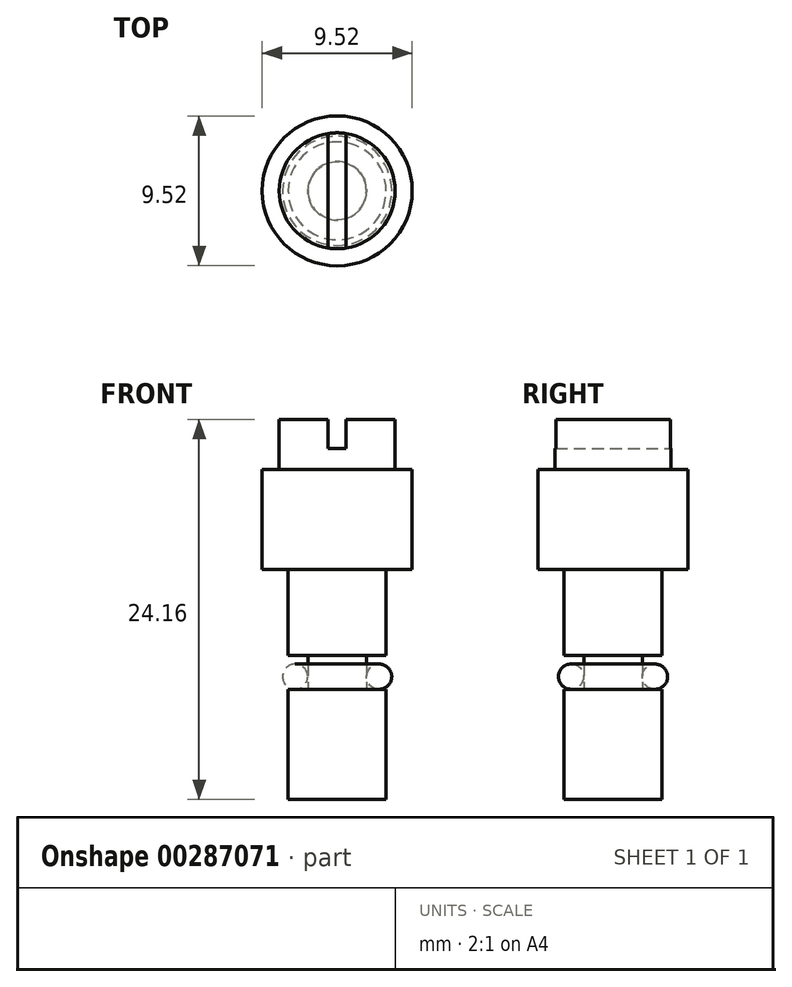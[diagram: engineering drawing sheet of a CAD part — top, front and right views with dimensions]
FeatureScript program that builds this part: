
annotation { "Feature Type Name" : "Feature", "Feature Type Description" : "" }
export const myFeature = defineFeature(function(context is Context, id is Id, definition is map)
    precondition{}
    {
        {
            var Q0;
            Q0=qCreatedBy(makeId("Front.planeOp"),FACE);
            var sketch = newSketch(context, id + "F0", { "sketchPlane" : qUnion([Q0])});
            skLineSegment(sketch, "E0", {"start": v(0, 0) * mm, "end": v(0, 26.45) * mm, "construction": true});
            skLineSegment(sketch, "E1", {"start": v(0, 0) * mm, "end": v(3.11, 0) * mm});
            skLineSegment(sketch, "E2", {"start": v(3.11, 0) * mm, "end": v(3.11, 7.01) * mm});
            skLineSegment(sketch, "E3", {"start": v(3.11, 7.01) * mm, "end": v(1.85, 7.01) * mm});
            skLineSegment(sketch, "E4", {"start": v(1.85, 7.01) * mm, "end": v(1.85, 9.17) * mm});
            skLineSegment(sketch, "E5", {"start": v(1.85, 9.17) * mm, "end": v(3.11, 9.17) * mm});
            skLineSegment(sketch, "E6", {"start": v(3.11, 9.17) * mm, "end": v(3.11, 14.63) * mm});
            skLineSegment(sketch, "E7", {"start": v(3.11, 14.63) * mm, "end": v(4.76, 14.63) * mm});
            skLineSegment(sketch, "E8", {"start": v(4.76, 14.63) * mm, "end": v(4.76, 20.98) * mm});
            skLineSegment(sketch, "E9", {"start": v(0, 24.16) * mm, "end": v(0, 0) * mm});
            skLineSegment(sketch, "E10", {"start": v(0, 24.16) * mm, "end": v(3.68, 24.16) * mm});
            skLineSegment(sketch, "E11", {"start": v(3.68, 24.16) * mm, "end": v(3.68, 20.98) * mm});
            skLineSegment(sketch, "E12", {"start": v(3.68, 20.98) * mm, "end": v(4.76, 20.98) * mm});
            skSolve(sketch);
        }
        {
            var Q0;
            Q0 = qSketchRegion(id + "F0", true);
            var Q1;
            Q1=sQuery(id+"F0.wireOp",EDGE,"E0");
            revolve(context, id + "F1", {"entities" : qUnion([Q0]), "axis" : qUnion([Q1]), "revolveType" : RevolveType.FULL});
        }
        {
            var Q0;
            Q0=makeQuery(id+"F1.opRevolve","SWEPT_FACE",FACE,{"disambiguationData":[OSD([sQuery(id+"F0.wireOp",EDGE,"E10")])]});
            var sketch = newSketch(context, id + "F2", { "sketchPlane" : qUnion([Q0])});
            skLineSegment(sketch, "E13.bottom", {"start": v(0.57, -4.76) * mm, "end": v(-0.57, -4.76) * mm});
            skLineSegment(sketch, "E13.top", {"start": v(0.57, 4.76) * mm, "end": v(-0.57, 4.76) * mm});
            skLineSegment(sketch, "E13.left", {"start": v(0.57, -4.76) * mm, "end": v(0.57, 4.76) * mm});
            skLineSegment(sketch, "E13.right", {"start": v(-0.57, -4.76) * mm, "end": v(-0.57, 4.76) * mm});
            skPoint(sketch, "E13.middle", {"position": v(0, 0) * mm});
            skSolve(sketch);
        }
        {
            var Q0;
            Q0 = qSketchRegion(id + "F2", true);
            extrude(context, id + "F3", {"entities" : qUnion([Q0]), "operationType" : NewBodyOperationType.REMOVE, "oppositeDirection" : true, "depth" : 1.85 * mm});
        }
        {
            var Q0;
            Q0=qCreatedBy(makeId("Front.planeOp"),FACE);
            var sketch = newSketch(context, id + "F4", { "sketchPlane" : qUnion([Q0])});
            skCircle(sketch, "E14", {"center": v(2.67, 7.81) * mm, "radius": 0.8 * mm});
            skLineSegment(sketch, "E15", {"start": v(0, 0) * mm, "end": v(0, 23.2) * mm, "construction": true});
            skSolve(sketch);
        }
        {
            var Q0;
            Q0 = qSketchRegion(id + "F4", true);
            var Q1;
            Q1=sQuery(id+"F4.wireOp",EDGE,"E15");
            revolve(context, id + "F5", {"operationType" : NewBodyOperationType.ADD, "entities" : qUnion([Q0]), "axis" : qUnion([Q1]), "revolveType" : RevolveType.FULL});
        }
    });
